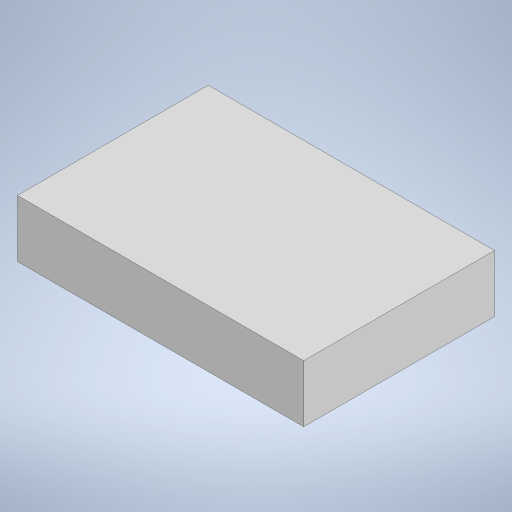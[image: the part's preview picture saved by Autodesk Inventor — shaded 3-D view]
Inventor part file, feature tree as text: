
AUTODESK INVENTOR PART (.ipt)
format: ipt  version: 2024 (Build 280153000, 153)  size: 236,544 bytes
history: native  units: mm
features: extrude x1, sketch x1
ambient origin geometry x8: Origin, YZ Plane, XZ Plane, XY Plane, X Axis, Y Axis, Z Axis, Center Point
bodies: Solid1 (feature_tree)
feature tree (2):
  extrude  "Extrusion1"  Depth=10.0mm
  sketch  "Sketch1"  dims[d0=15.0mm d1=10.0mm d2=3.0mm d3=0.0mm]
